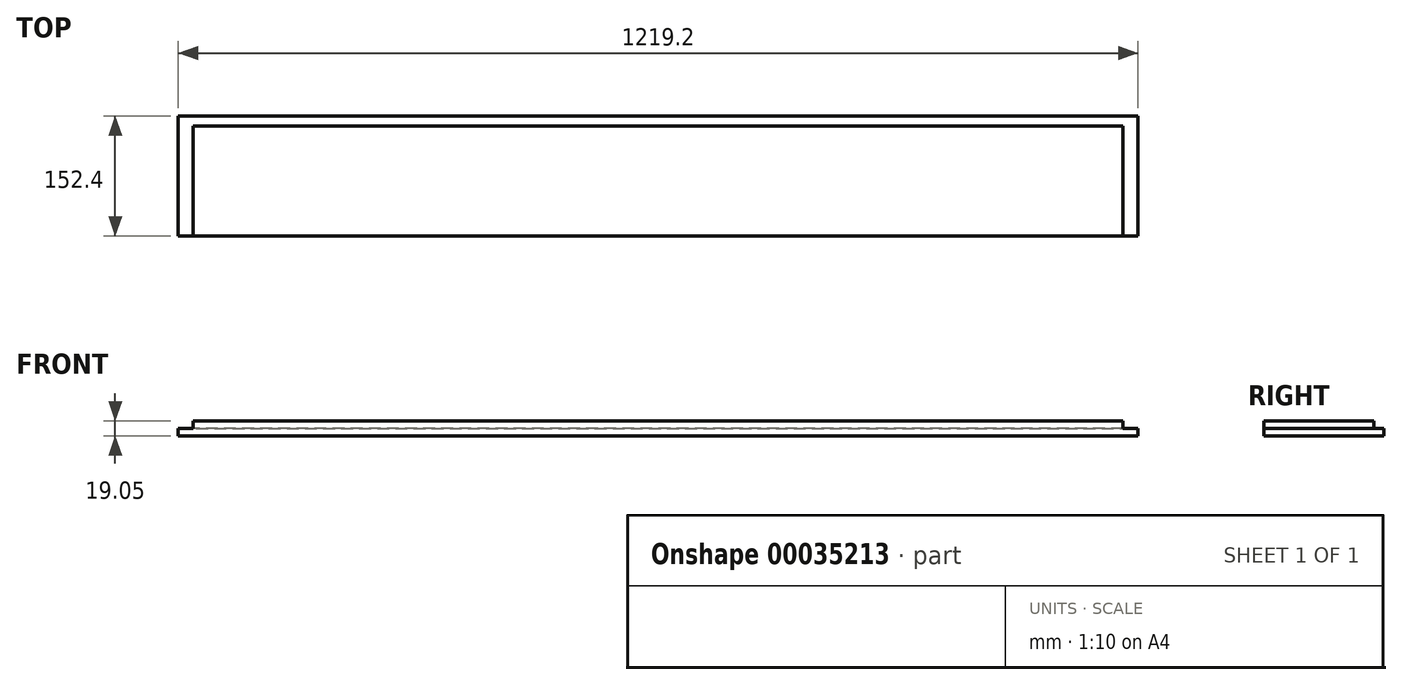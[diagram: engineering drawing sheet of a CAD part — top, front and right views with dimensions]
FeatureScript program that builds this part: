
annotation { "Feature Type Name" : "Feature", "Feature Type Description" : "" }
export const myFeature = defineFeature(function(context is Context, id is Id, definition is map)
    precondition{}
    {
        {
            var Q0;
            Q0=qCreatedBy(makeId("Top.planeOp"),FACE);
            var sketch = newSketch(context, id + "F0", { "sketchPlane" : qUnion([Q0])});
            skLineSegment(sketch, "E0.rect.bottom", {"start": v(-609.6, 0) * mm, "end": v(609.6, 0) * mm});
            skLineSegment(sketch, "E0.rect.top", {"start": v(-609.6, -152.4) * mm, "end": v(609.6, -152.4) * mm});
            skLineSegment(sketch, "E0.rect.left", {"start": v(-609.6, 0) * mm, "end": v(-609.6, -152.4) * mm});
            skLineSegment(sketch, "E0.rect.right", {"start": v(609.6, 0) * mm, "end": v(609.6, -152.4) * mm});
            skPoint(sketch, "E0.rect.middle", {"position": v(0, -76.2) * mm});
            skSolve(sketch);
        }
        {
            var Q0;
            Q0=makeQuery(id+"F0.imprint","IMPRINT",FACE,{"disambiguationData":[TD([[makeQuery(id+"F0.imprint","IMPRINT",EDGE,{"derivedFrom":sQuery(id+"F0.wireOp",EDGE,"E0.rect.bottom")}),-1.0]])]});
            extrude(context, id + "F1", {"entities" : qUnion([Q0]), "depth" : 19.05 * mm});
        }
        {
            var Q0;
            Q0=makeQuery(id+"F1.opExtrude","CAP_FACE",FACE,{"disambiguationData":[OSD([sQuery(id+"F0.wireOp",EDGE,"E0.rect.bottom"),sQuery(id+"F0.wireOp",EDGE,"E0.rect.top"),sQuery(id+"F0.wireOp",EDGE,"E0.rect.left"),sQuery(id+"F0.wireOp",EDGE,"E0.rect.right")])],"isStart":false});
            var sketch = newSketch(context, id + "F2", { "sketchPlane" : qUnion([Q0])});
            skLineSegment(sketch, "E1", {"start": v(-609.6, -152.4) * mm, "end": v(-609.6, 0) * mm});
            skLineSegment(sketch, "E2", {"start": v(-609.6, 0) * mm, "end": v(609.6, 0) * mm});
            skLineSegment(sketch, "E3", {"start": v(609.6, 0) * mm, "end": v(609.6, -152.4) * mm});
            skLineSegment(sketch, "E4", {"start": v(609.6, -152.4) * mm, "end": v(590.55, -152.4) * mm});
            skLineSegment(sketch, "E5", {"start": v(590.55, -152.4) * mm, "end": v(590.55, -12.7) * mm});
            skLineSegment(sketch, "E6", {"start": v(590.55, -12.7) * mm, "end": v(-590.55, -12.7) * mm});
            skLineSegment(sketch, "E7", {"start": v(-590.55, -12.7) * mm, "end": v(-590.55, -152.4) * mm});
            skLineSegment(sketch, "E8", {"start": v(-590.55, -152.4) * mm, "end": v(-609.6, -152.4) * mm});
            skSolve(sketch);
        }
        {
            var Q0;
            Q0=makeQuery(id+"F2.imprint","IMPRINT",FACE,{"disambiguationData":[TD([[makeQuery(id+"F2.imprint","IMPRINT",EDGE,{"derivedFrom":sQuery(id+"F2.wireOp",EDGE,"E1")}),1.0]])]});
            extrude(context, id + "F3", {"entities" : qUnion([Q0]), "operationType" : NewBodyOperationType.REMOVE, "oppositeDirection" : true, "depth" : 9.52 * mm});
        }
    });
